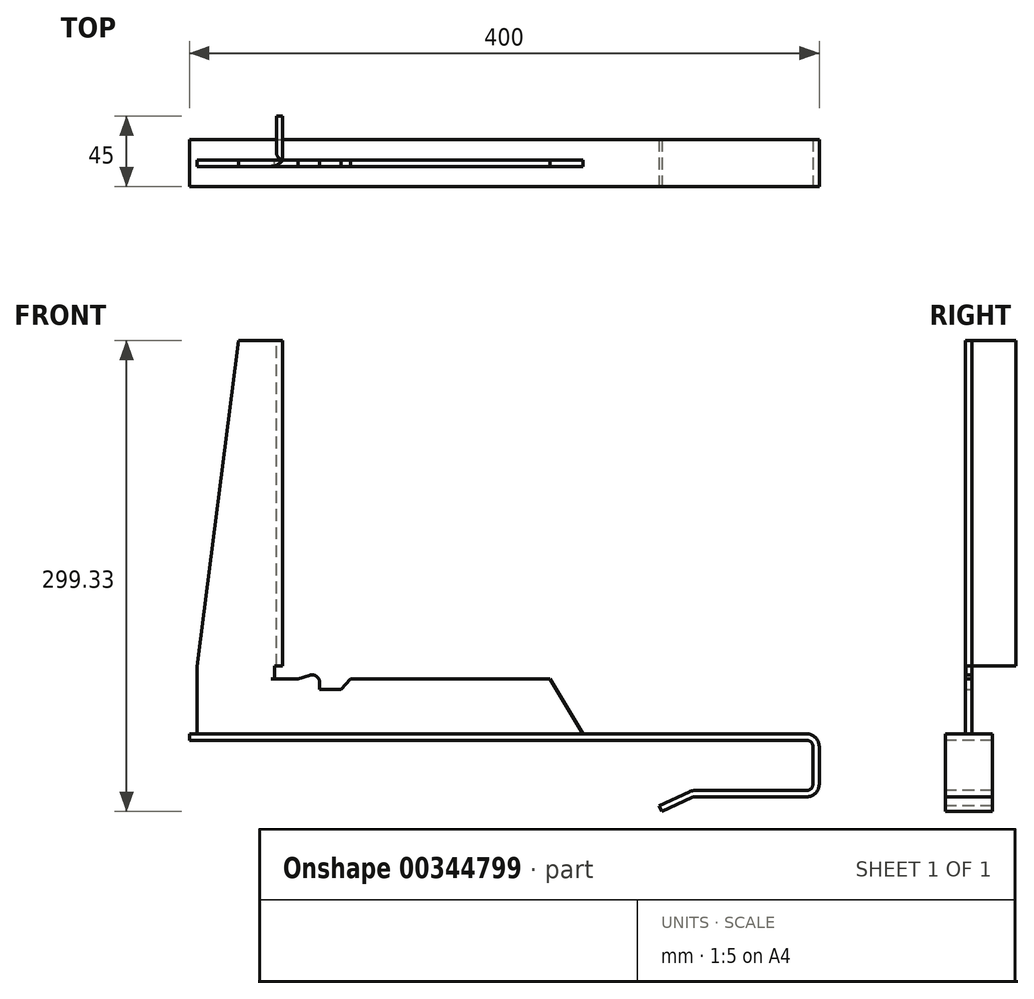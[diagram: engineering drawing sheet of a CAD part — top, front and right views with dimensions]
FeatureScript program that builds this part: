
annotation { "Feature Type Name" : "Feature", "Feature Type Description" : "" }
export const myFeature = defineFeature(function(context is Context, id is Id, definition is map)
    precondition{}
    {
        {
            var Q0;
            Q0=qCreatedBy(makeId("Front.planeOp"),FACE);
            var sketch = newSketch(context, id + "F0", { "sketchPlane" : qUnion([Q0])});
            skLineSegment(sketch, "E0", {"start": v(-211.32, 32.85) * mm, "end": v(180.68, 32.85) * mm});
            skLineSegment(sketch, "E1", {"start": v(188.68, 24.85) * mm, "end": v(188.68, 0.85) * mm});
            skLineSegment(sketch, "E2", {"start": v(180.68, -7.15) * mm, "end": v(109.57, -7.15) * mm});
            skLineSegment(sketch, "E3", {"start": v(107.88, -7.53) * mm, "end": v(88.68, -16.48) * mm});
            skLineSegment(sketch, "E4", {"start": v(-211.32, 32.85) * mm, "end": v(-211.32, 28.85) * mm});
            skLineSegment(sketch, "E5", {"start": v(-211.32, 28.85) * mm, "end": v(180.68, 28.85) * mm});
            skLineSegment(sketch, "E6", {"start": v(184.68, 24.85) * mm, "end": v(184.68, 0.85) * mm});
            skLineSegment(sketch, "E7.0", {"start": v(180.68, -3.15) * mm, "end": v(109.57, -3.15) * mm});
            skLineSegment(sketch, "E8.0", {"start": v(106.18, -3.9) * mm, "end": v(86.99, -12.85) * mm});
            skLineSegment(sketch, "E9", {"start": v(86.99, -12.85) * mm, "end": v(88.68, -16.48) * mm});
            skPoint(sketch, "E10.visualSharp", {"position": v(184.68, -3.15) * mm});
            skArc(sketch, "E10.filletArc", {"start": v(180.68, -3.15) * mm, "mid": v(183.5, -1.98) * mm, "end": v(184.68, 0.85) * mm});
            skPoint(sketch, "E11.visualSharp", {"position": v(188.68, -7.15) * mm});
            skArc(sketch, "E11.filletArc", {"start": v(180.68, -7.15) * mm, "mid": v(186.34, -4.81) * mm, "end": v(188.68, 0.85) * mm});
            skPoint(sketch, "E12.visualSharp", {"position": v(184.68, 28.85) * mm});
            skArc(sketch, "E12.filletArc", {"start": v(184.68, 24.85) * mm, "mid": v(183.5, 27.67) * mm, "end": v(180.68, 28.85) * mm});
            skPoint(sketch, "E13.visualSharp", {"position": v(188.68, 32.85) * mm});
            skArc(sketch, "E13.filletArc", {"start": v(188.68, 24.85) * mm, "mid": v(186.34, 30.5) * mm, "end": v(180.68, 32.85) * mm});
            skPoint(sketch, "E14.visualSharp", {"position": v(107.8, -3.15) * mm});
            skArc(sketch, "E14.filletArc", {"start": v(109.57, -3.15) * mm, "mid": v(107.83, -3.34) * mm, "end": v(106.18, -3.9) * mm});
            skPoint(sketch, "E15.visualSharp", {"position": v(108.68, -7.15) * mm});
            skArc(sketch, "E15.filletArc", {"start": v(109.57, -7.15) * mm, "mid": v(108.7, -7.25) * mm, "end": v(107.88, -7.53) * mm});
            skSolve(sketch);
        }
        {
            var Q0;
            Q0=makeQuery(id+"F0.imprint","IMPRINT",FACE,{"disambiguationData":[TD([[makeQuery(id+"F0.imprint","IMPRINT",EDGE,{"derivedFrom":sQuery(id+"F0.wireOp",EDGE,"E0")}),-1.0]])]});
            extrude(context, id + "F1", {"entities" : qUnion([Q0]), "endBound" : BoundingType.SYMMETRIC, "oppositeDirection" : true, "depth" : 30 * mm});
        }
        {
            var Q0;
            Q0=qCreatedBy(makeId("Front.planeOp"),FACE);
            var sketch = newSketch(context, id + "F2", { "sketchPlane" : qUnion([Q0])});
            skLineSegment(sketch, "E16", {"start": v(-206.32, 32.85) * mm, "end": v(38.68, 32.85) * mm});
            skLineSegment(sketch, "E17", {"start": v(38.68, 32.85) * mm, "end": v(17.57, 67.85) * mm});
            skLineSegment(sketch, "E18", {"start": v(17.57, 67.85) * mm, "end": v(-108.86, 67.85) * mm});
            skLineSegment(sketch, "E19", {"start": v(-108.86, 67.85) * mm, "end": v(-115.01, 61.19) * mm});
            skLineSegment(sketch, "E20", {"start": v(-115.01, 61.19) * mm, "end": v(-128.54, 61.19) * mm});
            skLineSegment(sketch, "E21", {"start": v(-128.54, 61.19) * mm, "end": v(-128.54, 65.35) * mm});
            skLineSegment(sketch, "E22", {"start": v(-135.03, 70.12) * mm, "end": v(-142.33, 67.85) * mm});
            skLineSegment(sketch, "E23", {"start": v(-142.33, 67.85) * mm, "end": v(-157.27, 67.85) * mm});
            skLineSegment(sketch, "E24", {"start": v(-157.27, 67.85) * mm, "end": v(-157.27, 76.1) * mm});
            skLineSegment(sketch, "E25", {"start": v(-157.27, 76.1) * mm, "end": v(-152.06, 76.1) * mm});
            skLineSegment(sketch, "E26", {"start": v(-152.06, 76.1) * mm, "end": v(-152.06, 282.85) * mm});
            skLineSegment(sketch, "E27", {"start": v(-152.06, 282.85) * mm, "end": v(-180.06, 282.85) * mm});
            skLineSegment(sketch, "E28", {"start": v(-180.06, 282.85) * mm, "end": v(-206.32, 75.67) * mm});
            skLineSegment(sketch, "E29", {"start": v(-206.32, 75.67) * mm, "end": v(-206.32, 32.85) * mm});
            skArc(sketch, "E30.filletArc", {"start": v(-128.54, 65.35) * mm, "mid": v(-130.58, 69.37) * mm, "end": v(-135.03, 70.12) * mm});
            skSolve(sketch);
        }
        {
            var Q0;
            Q0=makeQuery(id+"F2.imprint","IMPRINT",FACE,{"disambiguationData":[TD([[makeQuery(id+"F2.imprint","IMPRINT",EDGE,{"derivedFrom":sQuery(id+"F2.wireOp",EDGE,"E16")}),1.0]])]});
            extrude(context, id + "F3", {"entities" : qUnion([Q0]), "operationType" : NewBodyOperationType.ADD, "endBound" : BoundingType.SYMMETRIC, "depth" : 4 * mm});
        }
        {
            var Q0;
            Q0=makeQuery(id+"F3.opExtrude","SWEPT_FACE",FACE,{"disambiguationData":[OSD([sQuery(id+"F2.wireOp",EDGE,"E27")])]});
            var sketch = newSketch(context, id + "F4", { "sketchPlane" : qUnion([Q0])});
            skLineSegment(sketch, "E31.bottom", {"start": v(-152.06, 2) * mm, "end": v(-156.06, 2) * mm});
            skLineSegment(sketch, "E31.top", {"start": v(-152.06, 30) * mm, "end": v(-156.06, 30) * mm});
            skLineSegment(sketch, "E31.left", {"start": v(-152.06, 2) * mm, "end": v(-152.06, 30) * mm});
            skLineSegment(sketch, "E31.right", {"start": v(-156.06, 2) * mm, "end": v(-156.06, 30) * mm});
            skSolve(sketch);
        }
        {
            var Q0;
            Q0=makeQuery(id+"F4.imprint","IMPRINT",FACE,{"disambiguationData":[TD([[makeQuery(id+"F4.imprint","IMPRINT",EDGE,{"derivedFrom":sQuery(id+"F4.wireOp",EDGE,"E31.bottom")}),-1.0]])]});
            var Q1;
            Q1=makeQuery(id+"F3.opExtrude","CAP_VERTEX",VERTEX,{"disambiguationData":[OSD([sQuery(id+"F2.wireOp",EDGE,"E25"),sQuery(id+"F2.wireOp",EDGE,"E26")])],"isStart":true});
            var Q2;
            Q2=makeQuery(id+"F3.opExtrude","SWEPT_FACE",FACE,{"disambiguationData":[OSD([sQuery(id+"F2.wireOp",EDGE,"E25")])]});
            extrude(context, id + "F5", {"entities" : qUnion([Q0]), "endBound" : BoundingType.UP_TO_VERTEX, "oppositeDirection" : true, "endBoundEntityVertex" : qUnion([Q1]), "depth" : 25 * mm});
        }
        {
            var Q0;
            Q0=makeQuery(id+"F5.opExtrude","SWEPT_EDGE",EDGE,{"disambiguationData":[OSD([sQuery(id+"F2.wireOp",EDGE,"E27"),sQuery(id+"F4.wireOp",EDGE,"E31.bottom"),sQuery(id+"F4.wireOp",EDGE,"E31.right")])]});
            fillet(context, id + "F6", {"entities" : qUnion([Q0]), "radius" : 5 * mm, "tangentPropagation" : true, "allowEdgeOverflow" : false});
        }
        {
            var Q0;
            Q0=makeQuery(id+"F3.opExtrude","CAP_EDGE",EDGE,{"disambiguationData":[OSD([sQuery(id+"F2.wireOp",EDGE,"E26")])],"isStart":false});
            fillet(context, id + "F7", {"entities" : qUnion([Q0]), "radius" : 9 * mm, "tangentPropagation" : true, "allowEdgeOverflow" : false});
        }
    });
